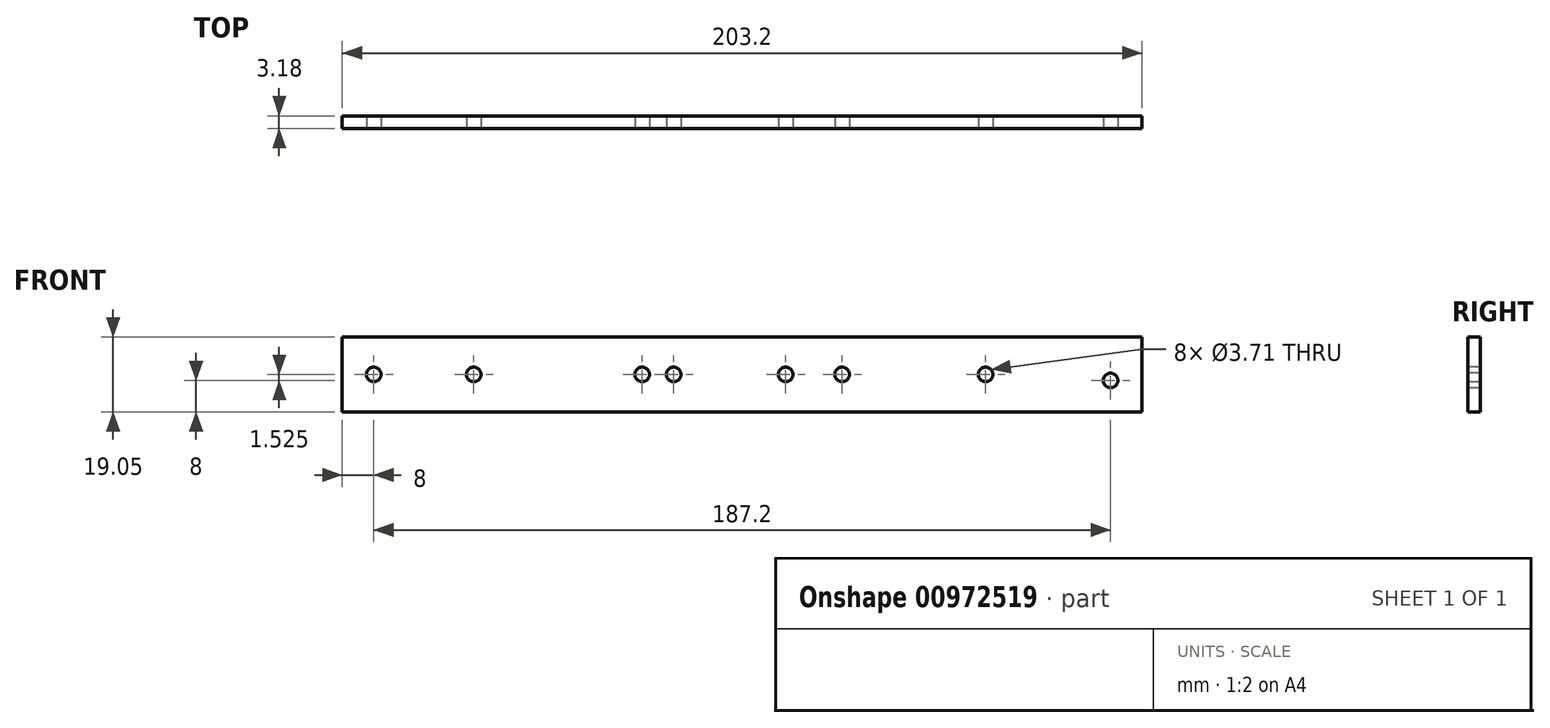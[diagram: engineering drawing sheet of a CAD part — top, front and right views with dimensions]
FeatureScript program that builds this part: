
annotation { "Feature Type Name" : "Feature", "Feature Type Description" : "" }
export const myFeature = defineFeature(function(context is Context, id is Id, definition is map)
    precondition{}
    {
        {
            var Q0;
            Q0=qCreatedBy(makeId("Front.planeOp"),FACE);
            var sketch = newSketch(context, id + "F0", { "sketchPlane" : qUnion([Q0])});
            skLineSegment(sketch, "E0.bottom", {"start": v(0, 0) * mm, "end": v(-203.2, 0) * mm});
            skLineSegment(sketch, "E0.top", {"start": v(0, 19.05) * mm, "end": v(-203.2, 19.05) * mm});
            skLineSegment(sketch, "E0.left", {"start": v(0, 0) * mm, "end": v(0, 19.05) * mm});
            skLineSegment(sketch, "E0.right", {"start": v(-203.2, 0) * mm, "end": v(-203.2, 19.05) * mm});
            skSolve(sketch);
        }
        {
            var Q0;
            Q0=makeQuery(id+"F0.imprint","IMPRINT",FACE,{"disambiguationData":[TD([[makeQuery(id+"F0.imprint","IMPRINT",EDGE,{"derivedFrom":sQuery(id+"F0.wireOp",EDGE,"E0.bottom")}),-1.0]])]});
            extrude(context, id + "F1", {"entities" : qUnion([Q0]), "depth" : 3.17 * mm, "offsetDistance" : 25.4 * mm});
        }
        {
            var Q0;
            Q0=makeQuery(id+"F1.opExtrude","CAP_FACE",FACE,{"disambiguationData":[OSD([sQuery(id+"F0.wireOp",EDGE,"E0.bottom"),sQuery(id+"F0.wireOp",EDGE,"E0.top"),sQuery(id+"F0.wireOp",EDGE,"E0.left"),sQuery(id+"F0.wireOp",EDGE,"E0.right")])],"isStart":false});
            var sketch = newSketch(context, id + "F2", { "sketchPlane" : qUnion([Q0])});
            skCircle(sketch, "E1", {"center": v(-195.2, 9.52) * mm, "radius": 1.86 * mm});
            skPoint(sketch, "E1.centerSnap0", {"position": v(-203.2, 9.52) * mm});
            skCircle(sketch, "E2", {"center": v(-169.8, 9.52) * mm, "radius": 1.86 * mm});
            skCircle(sketch, "E3", {"center": v(-127, 9.52) * mm, "radius": 1.86 * mm});
            skCircle(sketch, "E4", {"center": v(-119, 9.52) * mm, "radius": 1.86 * mm});
            skCircle(sketch, "E5", {"center": v(-90.55, 9.52) * mm, "radius": 1.86 * mm});
            skCircle(sketch, "E6", {"center": v(-76.2, 9.53) * mm, "radius": 1.86 * mm});
            skCircle(sketch, "E7", {"center": v(-39.75, 9.53) * mm, "radius": 1.86 * mm});
            skCircle(sketch, "E8", {"center": v(-8, 8) * mm, "radius": 1.86 * mm});
            skSolve(sketch);
        }
        {
            var Q0;
            Q0 = qSketchRegion(id + "F2", true);
            extrude(context, id + "F3", {"entities" : qUnion([Q0]), "operationType" : NewBodyOperationType.REMOVE, "oppositeDirection" : true, "depth" : 25.4 * mm, "offsetDistance" : 25.4 * mm});
        }
    });
